# Revit family: QF_ELECTROLUXPROFESSIONAL_1LSNTF_WS6-20_E
name_source: partatom
category: Attrezzature speciali
units: mm (PartAtom-declared; Revit-internal decimal feet)

## family parameters
Basato su piano di lavoro = No
Condiviso = No
Punto di calcolo locali = No
Quota connettore circolare = Usa diametro
Sempre verticale = Sì
Taglio con vuoti quando caricato = No
Tipo di parte = Normale

## types (32) — shared parameters
Depth = 915.5 mm  [stored 3.00361 ft]
Depth Actual = 915 mm  [stored 3.00197 ft]
Height = 1346.8 mm  [stored 4.41864 ft]
Height Actual = 1345 mm
Latent Heat Output = 0.0
Length Actual = 750 mm  [stored 2.46063 ft]
Modello = WS6-20
Produttore = Electrolux Professional
Sensible Heat Output = 0.0
URL = www.electroluxprofessional.com
Weight = 221
Width = 750 mm  [stored 2.46063 ft]
zero-valued in all types: Gas KW, Prospetto di default, Steam Pounds per Hour

## per-type parameters (varying)
| type | Cycle | Descrizione | Item Number | Phase | Volts | Watts |
| 9867830288 | 60 Hz | WASHER WS6-20 20KG NO HEAT 220-240/60/1N COMPASS PRO 6G07 ML 2xWATER POWDER+5xLIQ. EL.VALV.OPEN SILVER 2.I/O DISCON. STO | 1LT6DA | 1 | 240 V | 800 W |
| 9867830114 | 50 Hz | WASHER WS6-20 20KG EL 13KW 380-415/50/3N COMPASS PRO 6G01 ML 2xWATER POWDER+5xLIQ. VALV.OPEN SILVER 2.I/O DISCON. STOP | 1LSP5U | 3 | 415 V | 13500 W |
| 9867830213 | 50 Hz | WASHER WS6-20 20KG EL 13KW 380-415/50/3 COMPASS PRO 6G01 ML 2xWATER POWDER+5xLIQ. VALV.OPEN SILVER 2.I/O QC TRAFO DISCON | 1LSPHC | 3 | 415 V | 13500 W |
| 9867830276 | 50 Hz | WASHER WS6-20 20KG EL 13KW 380-415/50/3N COMPASS PRO 6G01 ML 2xWATER POWDER+5xLIQ. VALV.CLOSED SILVER 2.I/O DISCON. STOP | 1LM0B7 | 3 | 415 V | 13500 W |
| 9867830201 | 50 Hz | WASHER WS6-20 20KG MOP 13KW 220-240/50/3 COMPASS PRO 6M14 ML 2xWATER POWDER+5xLIQ. EL.VALV.OPEN SILVER 2.I/O QC DISCON. | 1L0GTJ | 3 | 240 V | 13500 W |
| 9867830211 | 50 Hz | WASHER WS6-20 20KG NO HEAT 200/50/60/3 COMPASS PRO 6L41 JP,EN 2xWATER POWDER+5xLIQ. VALV.OPEN SILVER 2.I/O DISCON. | 1L827P | 3 | 200 V | 1500 W |
| 9867830116 | 50 Hz | WASHER WS6-20 20KG MOP 13KW 380-415/50/3N COMPASS PRO 6F01 ML 2xWATER POWDER+ED EL.VALV.OPEN SST DISCON. STOP LID | 1LSP5V | 3 | 415 V | 13500 W |
| 9867830149 | 50 Hz | WASHER WS6-20 20KG EL 13KW 380-415/50/3N COMPASS PRO 6G01 CH-EN 2xWATER POWDER VALV.OPEN SILVER DISCON. STOP | 1LA1AG | 3 | 415 V | 13500 W |
| 9867830179 | 50 Hz | WASHER WS6-20 20KG NO HEAT 220-240/50/1N COMPASS PRO 6L01 ML 2xWATER POWDER+5xLIQ. VALV.OPEN SILVER ELS-NETW. 2.I/O DISC | 1LSPDT | 1 | 240 V | 800 W |
| 9867830186 | 60 Hz | WASHER WS6-20 20KG EL 13KW 220-240/60/1N COMPASS PRO 6G07 ML 2xWATER POWDER+5xLIQ. VALV.OPEN SILVER 2.I/O QC DISCON. STO | 1LA22R | 1 | 240 V | 13500 W |
| 9867830244 | 50 Hz | WASHER WS6-20 20KG NO HEAT 220-240/50/1N COMPASS PRO 6L01 ML 2xWATER POWDER+5xLIQ. VALV.OPEN SILVER 2.I/O DISCON. | 1L82AG | 1 | 240 V | 800 W |
| 9867830113 | 50 Hz | WASHER WS6-20 20KG NO HEAT 220-240/50/1N COMPASS PRO 6L01 ML 2xWATER POWDER+5xLIQ. VALV.OPEN SST/SILVER ELS-NETW. EXT.PM | 1L824E | 1 | 240 V | 800 W |
| 9867830163 | 60 Hz | WASHER WS6-20 20KG NO HEAT 208-240/60/1 COMPASS PRO 6G01 ML 2xWATER POWDER+5xLIQ. VALV.CLOSED SILVER 2.I/O STOP | 1LSPAR | 1 | 240 V | 800 W |
| 9867830153 | 50 Hz | WASHER WS6-20 20KG MOP 13KW 380-400/220-230/50/3N/3 COMPASS PRO 6M14 ML 2xWATER POWDER+5xLIQ. EL.VALV.OPEN SILVER 2.I/O | 1LA1B0 | 3 | 415 V | 13500 W |
| 9867830193 | 60 Hz | WASHER WS6-20 20KG NO HEAT 208-240/60/1 COMPASS PRO 6L01 ML 2xWATER POWDER+5xLIQ. VALV.OPEN SILVER ELS-NETW. 2.I/O | 1LSPE7 | 1 | 240 V | 800 W |
| 9867830217 | 50 Hz | WASHER WS6-20 20KG NO HEAT 200/50/60/3 COMPASS PRO 6L41 JP,EN 2xWATER 5xLIQ. VALV.OPEN SST/SILVER 2.I/O DISCON. | 1L0GXP | 3 | 200 V | 1500 W |
| 9867830190 | 60 Hz | WASHER WS6-20 20KG NO HEAT 220-240/60/3 COMPASS PRO 6L01 ML 2xWATER POWDER VALV.OPEN SST DISCON. | 1L999D | 3 | 220 V | 800 W |
| 9867830115 | 50 Hz | WASHER WS6-20 20KG EL 13KW 380-415/50/3N COMPASS PRO 6H01 ML 2xWATER POWDER+5xLIQ. VALV.OPEN SILVER 2.I/O DISCON. STOP | 1L824F | 3 | 415 V | 13500 W |
| 9867830145 | 50 Hz | WASHER WS6-20 20KG EL 13KW 380-415/220-240/50/3N/1 COMPASS PRO 6G01 ML 2xWATER POWDER+5xLIQ. VALV.OPEN SILVER 2.I/O DISC | 1L0GCB | 3 | 415 V | 13500 W |
| 9867830155 | 50 Hz | WASHER WS6-20 20KG NO HEAT 200/50/60/3 COMPASS PRO 6L41 JP,EN 2xWATER 5xLIQ. VALV.OPEN SILVER 2.I/O DISCON. | 1LA1BC | 3 | 200 V | 1500 W |
| 9867830185 | 60 Hz | WASHER WS6-20 20KG EL 13KW 440/60/3 COMPASS PRO 6G07 ML 2xWATER POWDER+5xLIQ. VALV.OPEN SST/SILVER 2.I/O QC TRAFO DISCON | 1LA22E | 3 | 440 V | 13700 W |
| 9867830188 | 60 Hz | WASHER WS6-20 20KG NO HEAT 220-240/60/3 COMPASS PRO 6L01 ML 2xWATER POWDER VALV.OPEN SILVER DISCON. | 1L0GLM | 3 | 220 V | 800 W |
| 9867830282 | 60 Hz | WASHER WS6-20 20KG EL 13KW 220-240/60/1N COMPASS PRO 6G01 ML 2xWATER POWDER+5xLIQ. VALV.OPEN SILVER 2.I/O DISCON. STOP | 1L0HE4 | 1 | 240 V | 13500 W |
| 9867830292 | 50 Hz | WASHER WS6-20 20KG EL 13KW 380-415/50/3 COMPASS PRO 6G07 ML 2xWATER POWDER+5xLIQ. VALV.CLOSED SST 2.I/O TRAFO DISCON. ST | 1L0HJ7 | 3 | 415 V | 13500 W |
| 9867830255 | 60 Hz | WASHER WS6-20 20KG EL 13KW 208-240/60/3 COMPASS PRO 6H12 ML 2xWATER POWDER+5xLIQ. VALV.OPEN SST 2.I/O DISCON. STOP | 1LSPSS | 3 | 240 V | 13500 W |
| 9867830285 | 50 Hz | WASHER WS6-20 20KG EL 13KW 380-415/50/3N COMPASS PRO 6G01 ML 2xWATER POWDER+5xLIQ. VALV.CLOSED SST 2.I/O DISCON. STOP | 1L82DE | 3 | 415 V | 13500 W |
| 9867830112 | 50 Hz | WASHER WS6-20 20KG NO HEAT 220-240/50/1N COMPASS PRO 6L01 ML 2xWATER POWDER+5xLIQ. VALV.OPEN SILVER EXT.PM. 2.I/O DISCON | 1LSP3P | 1 | 240 V | 800 W |
| 9867830127 | 50 Hz | WASHER WS6-20 20KG EL 13KW 380-415/50/3N COMPASS PRO 6G01 ML 2xWATER POWDER+5xLIQ. VALV.OPEN SST/SILVER 2.I/O DISCON. ST | 1L821P | 3 | 415 V | 13500 W |
| 9867830230 | 60 Hz | WASHER WS6-20 20KG EL 13KW 220-240/60/3 COMPASS PRO 6G07 SE 2xWATER POWDER+5xLIQ. VALV.OPEN SILVER 2.I/O QC DISCON. STOP | 1L0H0U | 3 | 240 V | 13500 W |
| 9867830200 | 60 Hz | WASHER WS6-20 20KG EL 13KW 480/60/3 COMPASS PRO 6G07 ML 2xWATER POWDER+5xLIQ. VALV.OPEN SILVER 2.I/O TRAFO DISCON. STOP | 1L0GTH | 3 | 480 V | 13700 W |
| 9867830290 | 60 Hz | WASHER WS6-20 20KG NO HEAT 220/60/3 COMPASS PRO 6G07 ML 2xWATER POWDER+5xLIQ. EL.VALV.OPEN SILVER 2.I/O DISCON. STOP | 1L0HGX | 3 | 220 V | 800 W |
| 9867830278 | 60 Hz | WASHER WS6-20 20KG EL 13KW 480/60/3 COMPASS PRO 6G07 ML 2xWATER POWDER+5xLIQ. VALV.OPEN SST 2.I/O TRAFO DISCON. STOP | 1LT65G | 3 | 480 V | 13600 W |

note: [stored X ft] marks values corroborated as IEEE doubles in the binary element streams (Revit-internal decimal feet)

## geometry (parser evidence)
native form markers: Sweep x4
no freeform markers — native parametric forms only
